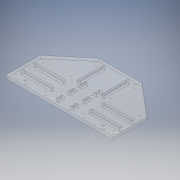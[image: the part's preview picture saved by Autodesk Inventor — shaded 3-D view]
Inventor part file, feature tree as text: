
AUTODESK INVENTOR PART (.ipt)
format: ipt  version: 2019 (Build 230136000, 136)  size: 221,184 bytes
history: native  units: mm
features: extrude x1
ambient origin geometry x8: Origin, YZ Plane, XZ Plane, XY Plane, X Axis, Y Axis, Z Axis, Center Point
bodies: Body1 (feature_tree)
feature tree (1):
  extrude  "Extrusion2"  Depth=6.0mm TaperAngle=0.0deg
